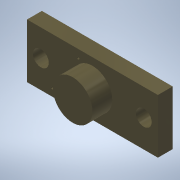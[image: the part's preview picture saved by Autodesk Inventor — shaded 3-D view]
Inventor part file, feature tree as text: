
AUTODESK INVENTOR PART (.ipt)
format: ipt  version: 2020 (Build 240168000, 168)  size: 122,880 bytes
history: mixed  units: in
note: dims shown in document units (in); Inventor stores cm internally (conversion verified against a paired STEP export)
features: other x1, extrude x1, sketch x1, projected_geometry x1, imported_body x1
ambient origin geometry x8: Origin, YZ Plane, XZ Plane, XY Plane, X Axis, Y Axis, Z Axis, Center Point
bodies: Solid1 (imported_parasolid)
feature tree (5):
  other  "Board"
  extrude  "Extrusion1"  Depth=0.0787in TaperAngle=0.0deg
  sketch  "Sketch1"  dims[d0=0.1575in d1=0.0787in d2=0.0in]
  projected_geometry  "Projected Loop1"
  imported_body  NMx_Import_Brep_tag  [imported B-rep: ~18 faces, bbox_mm=[13.238, 5.492, 3.5]]
